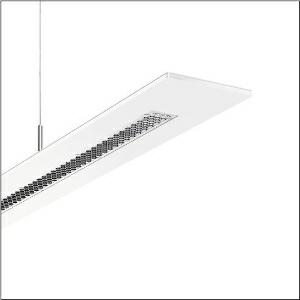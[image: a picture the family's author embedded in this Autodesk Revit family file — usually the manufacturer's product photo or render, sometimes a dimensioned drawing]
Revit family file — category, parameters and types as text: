
# Revit family: arktika_r__21_5mb251dl30840_e160
name_source: partatom
category: Lighting Fixtures
units: mm (PartAtom-declared; Revit-internal decimal feet)

## family parameters
Cut with Voids When Loaded = No
Host = Face
Light Source = No
Part Type = Normal
Room Calculation Point = No
Round Connector Dimension = Use Diameter
Shared = No

## types (1)
- --- (1 x LED 4000K / CRI = 80 (unbekannt), 4400 lm, 4000K)
    Apparent Load = 34 VA
    CIE Flux Codes = 81 100 100 79 100
    Color Rendering = 80
    Color Temperature = 4000K
    Default Elevation = 1800 mm
    Description = Arktika® 21, office luminaire, primary anti-glare with honeycomb louvre, of plastic, aluminium vaporised, highly specular, light emission: direct/indirect distribution, primary light characteristic: symmetric, installation type: suspended mounting, LED, rated luminous flux: 4.400lm, luminous efficacy: 131lm/W, light colour: 840, colour temperature: 4000K, control gear: DALI, with terminal, 3+2-pole, max. 2.5mm², mains connection: 220..240V, AC, 50/60Hz, rated input power: 34W, housing, of aluminium, powder-coated, traffic white (RAL 9016), 1-length, length: 1.250mm, width: 120mm, height: 8mm, protection rating (complete): IP20, insulation class (complete): insulation class II (safety insulation), certification: CE, ENEC, VDE, packaging unit: 1 piece
    Height = 8 mm  [stored 0.0262467 ft]
    Lamp = 1 x LED 4000K / CRI >= 80 (unbekannt)
    Lamp Light Flux = 4400 lm
    Lamp count = 1
    Length = 1250 mm
    Luminous efficacy = 131 lm/W
    Manufacturer = Siteco
    ModVariant = No
    Model = 5MB251DL30840
    Mounting Place = Ceiling
    Mounting Type = Pendant
    Number of Poles = 1
    OnlyDefault = Yes
    Power Factor = 1
    Product Name = Arktika® 21
    Product group = office luminaire | ceiling pendant
    ProductGroupID = 903
    Protection Class = Protection class II
    Protection Degree = IP 20
    RLX_Detail_Level = 1
    RLX_Emergency_Light_Flux = 0 lm
    RLX_Emergency_Type = 0
    RLX_Emergency_Type_DB = No
    RlxData = <blob elided: 39249 chars, md5=ba9de683>
    Socket = socket
    Standby Power = 0 W
    System Light Flux = 4400 lm
    System Power = 34 W
    Type Comments = factory setting: luminous flux: 100 % | dim-lin: 254 | 665 mA
    Type Image = l_1006128.jpg
    URL = http://relux.com
    VarID = @adj_219905
    Voltage = 0 V
    Weight = 0.00 kg
    Width = 120 mm

note: [stored X ft] marks values corroborated as IEEE doubles in the binary element streams (Revit-internal decimal feet)

## geometry (parser evidence)
native form markers: Blend x4, Sweep x11
no freeform markers — native parametric forms only
